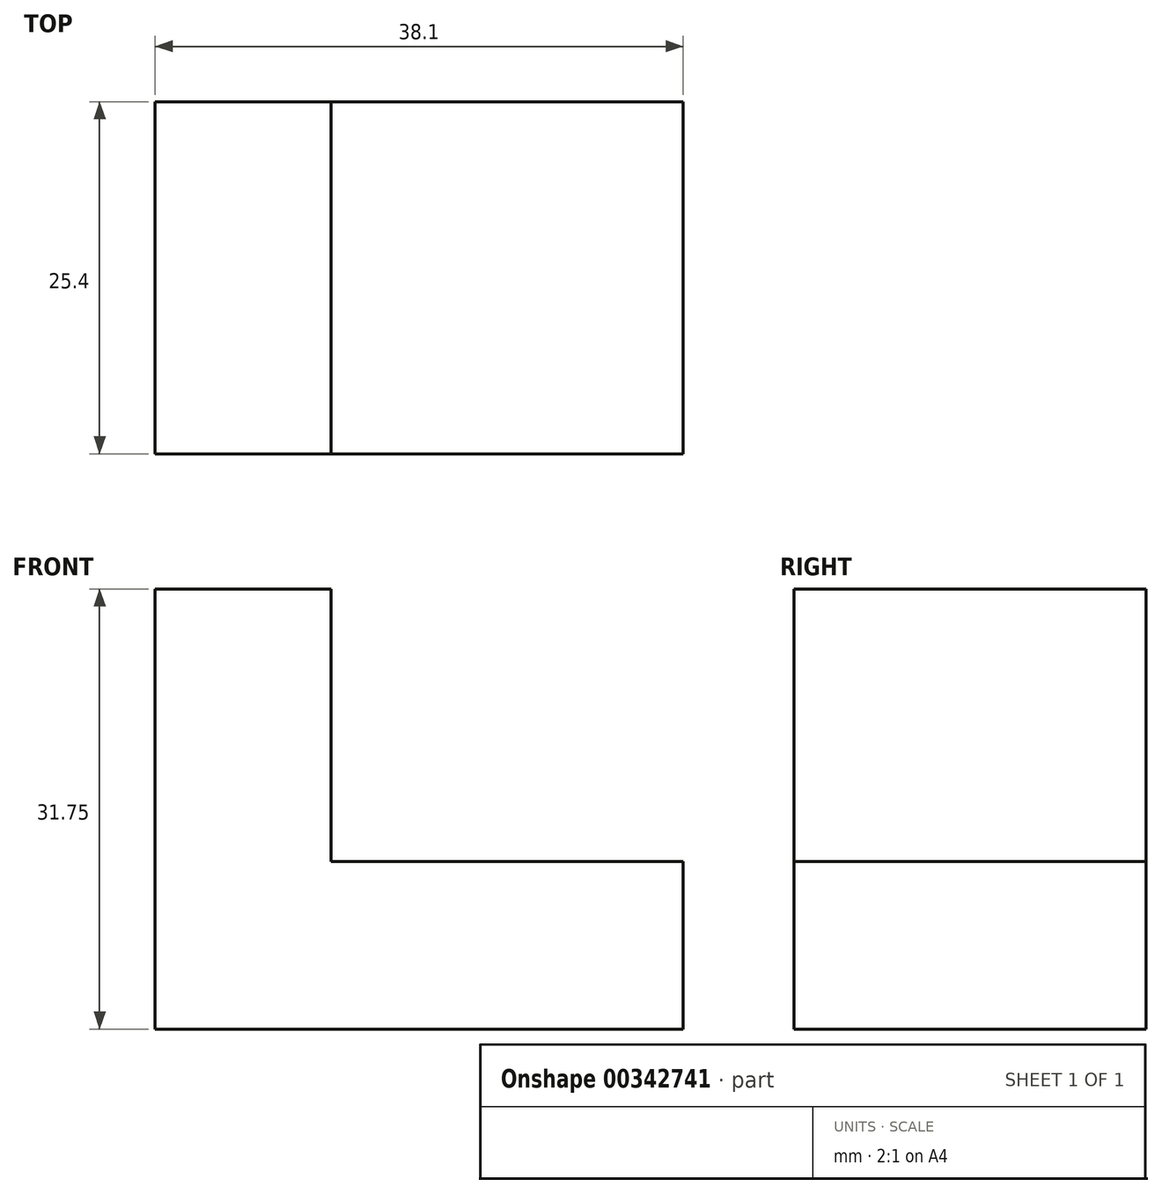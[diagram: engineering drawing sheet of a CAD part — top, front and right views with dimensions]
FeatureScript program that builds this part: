
annotation { "Feature Type Name" : "Feature", "Feature Type Description" : "" }
export const myFeature = defineFeature(function(context is Context, id is Id, definition is map)
    precondition{}
    {
        {
            var Q0;
            Q0=qCreatedBy(makeId("Front.planeOp"),FACE);
            var sketch = newSketch(context, id + "F0", { "sketchPlane" : qUnion([Q0])});
            skLineSegment(sketch, "E0", {"start": v(0, 0) * mm, "end": v(0, 31.75) * mm});
            skLineSegment(sketch, "E1", {"start": v(0, 31.75) * mm, "end": v(12.7, 31.75) * mm});
            skLineSegment(sketch, "E2", {"start": v(12.7, 31.75) * mm, "end": v(12.7, 12.09) * mm});
            skLineSegment(sketch, "E3", {"start": v(12.7, 12.09) * mm, "end": v(38.1, 12.09) * mm});
            skLineSegment(sketch, "E4", {"start": v(38.1, 12.09) * mm, "end": v(38.1, 0) * mm});
            skLineSegment(sketch, "E5", {"start": v(38.1, 0) * mm, "end": v(0, 0) * mm});
            skSolve(sketch);
        }
        {
            var Q0;
            Q0 = qSketchRegion(id + "F0", true);
            extrude(context, id + "F1", {"entities" : qUnion([Q0]), "oppositeDirection" : true, "depth" : 25.4 * mm});
        }
    });
